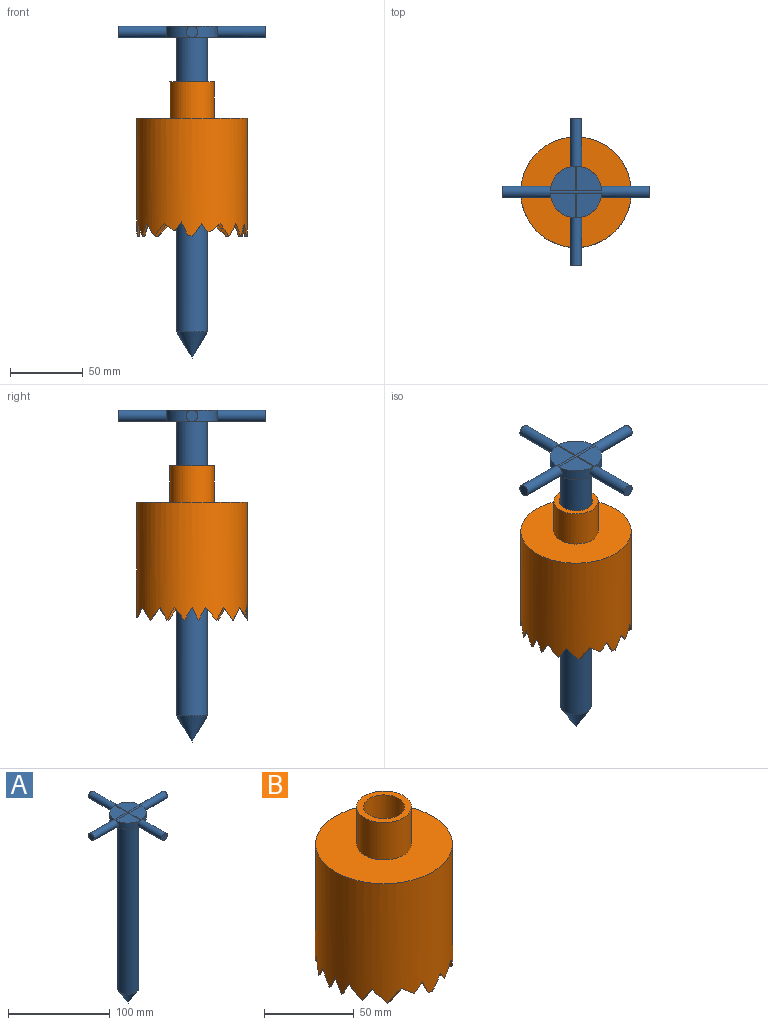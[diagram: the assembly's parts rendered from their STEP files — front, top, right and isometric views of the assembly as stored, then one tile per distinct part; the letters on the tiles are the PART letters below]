
ASSEMBLY  parts=2 mates=1
PART A: 21 faces, bbox 101.6x101.6x228.9 mm
  f0: cylinder r=10.67mm len=203.2mm, axis (0,0,-1), area 13619.6mm2, adj f9,f10,f11,f12,f13,f14,f15,f18
  f1: cylinder r=17.78mm len=17.4mm, axis (0,0,-1), area 163.7mm2, adj f7,f11,f14,f18
  f2: cylinder r=17.78mm len=17.4mm, axis (0,0,-1), area 163.7mm2, adj f8,f12,f13,f18
  f3: cylinder r=17.78mm len=17.4mm, axis (0,0,-1), area 163.7mm2, adj f6,f10,f13,f18
  f4: cylinder r=17.78mm len=17.4mm, axis (0,0,-1), area 163.7mm2, adj f5,f9,f14,f18
  f5: plane 17.4x16.82mm, normal (0,0,1), area 225.4mm2, adj f4,f14,f18
  f6: plane 17.4x16.82mm, normal (0,0,1), area 225.4mm2, adj f3,f13,f18
  f7: plane 17.4x16.82mm, normal (0,0,1), area 225.4mm2, adj f1,f14,f18
  f8: plane 17.4x16.82mm, normal (0,0,1), area 225.4mm2, adj f2,f13,f18
  f9: plane 16.45x16.32mm, normal (0,0,-1), area 139.7mm2, adj f0,f4,f14,f18
  f10: plane 16.45x16.32mm, normal (0,0,-1), area 139.7mm2, adj f0,f3,f13,f18
  f11: plane 16.45x16.32mm, normal (0,0,-1), area 139.7mm2, adj f0,f1,f14,f18
  f12: plane 16.45x16.32mm, normal (0,0,-1), area 139.7mm2, adj f0,f2,f13,f18
  f13: cylinder r=3.92mm len=49.85mm, axis (0,1,0), area 850.3mm2, adj f0,f2,f3,f6,f8,f10,f12,f16
  f14: cylinder r=3.92mm len=49.85mm, axis (0,1,0), area 850.3mm2, adj f0,f1,f4,f5,f7,f9,f11,f17
  f15: cone r=0mm half-angle=30.7deg, axis (0,0,1), area 699.5mm2, adj f0
  f16: plane 7.85x7.85mm, normal (0,-1,0), area 48.4mm2, adj f13
  f17: plane 7.85x7.85mm, normal (0,1,0), area 48.4mm2, adj f14
  f18: cylinder r=4mm len=101.6mm, axis (-1,0,0), area 1779.7mm2, adj f0,f1,f2,f3,f4,f5,f6,f7
  f19: plane 7.99x7.99mm, normal (1,0,0), area 50.2mm2, adj f18
  f20: plane 7.99x7.99mm, normal (-1,0,0), area 50.2mm2, adj f18
PART B: 53 faces, bbox 76.2x76.2x106.7 mm
  f0: plane 8.48x5.49mm, normal (0,0.86,-0.51), area 17.7mm2, adj f2,f3,f25,f51
  f1: plane 9.65x6.27mm, normal (0,0.86,-0.51), area 21mm2, adj f2,f3,f30,f50
  f2: cylinder r=38.1mm len=81.28mm, axis (0,0,-1), area 18310.4mm2, adj f0,f1,f4,f5,f6,f9,f13,f14
  f3: cylinder r=36.83mm len=76.2mm, axis (0,0,1), area 16479.2mm2, adj f0,f1,f4,f5,f6,f7,f8,f13
  f4: plane 10.91x7.39mm, normal (0,-0.92,-0.4), area 29.2mm2, adj f2,f3,f14,f46
  f5: plane 7.32x4.48mm, normal (0,-0.9,-0.44), area 15.4mm2, adj f2,f3,f44,f47
  f6: plane 5.6x3.34mm, normal (0,-0.9,-0.44), area 11.6mm2, adj f2,f3,f7,f45,f48
  f7: plane 0.13x0.06mm, normal (1,0,0), area 0mm2, adj f3,f6,f45
  f8: plane 73.66x73.66mm, normal (0,0,-1), area 3851mm2, adj f3,f12
  f9: plane 76.2x76.2mm, normal (0,0,1), area 3830.7mm2, adj f2,f10
  f10: cylinder r=15.24mm len=30.48mm, axis (0,0,-1), area 2432.2mm2, adj f9,f11
  f11: plane 30.48x30.48mm, normal (0,0,1), area 319.2mm2, adj f10,f12
  f12: cylinder r=11.43mm len=30.48mm, axis (0,0,1), area 2189mm2, adj f8,f11
  f13: plane 4.07x2.49mm, normal (0,0.86,-0.51), area 8.8mm2, adj f2,f3,f26,f52
  f14: plane 11.45x9.22mm, normal (0,0.86,-0.51), area 25.9mm2, adj f2,f3,f4,f15
  f15: plane 9.22x8.05mm, normal (0,-0.81,-0.59), area 19.9mm2, adj f2,f3,f14,f16
  f16: plane 9.22x4.67mm, normal (0,0.89,-0.45), area 15.4mm2, adj f2,f3,f15,f17
  f17: plane 9.22x5.19mm, normal (0,-0.87,-0.49), area 14.6mm2, adj f2,f3,f16,f18
  f18: plane 9.22x6.92mm, normal (0,0.8,-0.6), area 15.1mm2, adj f2,f3,f17,f19
  f19: plane 9.22x5.17mm, normal (0,-0.87,-0.49), area 13.5mm2, adj f2,f3,f18,f20
  f20: plane 9.24x4.53mm, normal (0,0.9,-0.44), area 13.1mm2, adj f2,f3,f19,f21
  f21: plane 9.22x4.67mm, normal (0,-0.89,-0.45), area 13.4mm2, adj f2,f3,f20,f22
  f22: plane 9.22x7.78mm, normal (0,0.76,-0.65), area 16.4mm2, adj f2,f3,f21,f23
  f23: plane 9.22x4.67mm, normal (0,-0.89,-0.45), area 15.3mm2, adj f2,f3,f22,f24
  f24: plane 9.22x7.88mm, normal (0,0.81,-0.59), area 19.6mm2, adj f2,f3,f23,f25
  f25: plane 9.22x8.81mm, normal (0,-0.9,-0.44), area 22.9mm2, adj f0,f2,f3,f24
  f26: plane 2.52x1.27mm, normal (-1,0,0), area 0.7mm2, adj f2,f3,f13,f31,f49
  f27: plane 11.7x8.64mm, normal (0,0.84,-0.54), area 25mm2, adj f2,f3,f28,f33
  f28: plane 3.37x0.15mm, normal (0,-0.92,-0.4), area 0.5mm2, adj f2,f3,f27,f44
  f29: plane 1.91x0.28mm, normal (0,0.8,-0.6), area 0.6mm2, adj f3,f32,f34,f35
  f30: plane 5.06x3.27mm, normal (0,-0.9,-0.44), area 8.9mm2, adj f1,f2,f3,f34
  f31: plane 2.07x1.64mm, normal (0,0.86,-0.51), area 1.9mm2, adj f3,f26,f49
  f32: plane 0.33x0.21mm, normal (-1,0,0), area 0mm2, adj f29,f34,f35
  f33: plane 8.67x7.36mm, normal (0,-0.83,-0.55), area 18.4mm2, adj f2,f3,f27,f43
  f34: plane 5.83x5.68mm, normal (0,-0.9,-0.44), area 13.2mm2, adj f2,f3,f29,f30,f32,f35
  f35: plane 8.87x6.38mm, normal (0,0.87,-0.49), area 17.3mm2, adj f2,f3,f29,f32,f34,f36
  f36: plane 8.87x5.37mm, normal (0,-0.86,-0.52), area 15.8mm2, adj f2,f3,f35,f37
  f37: plane 8.87x5.01mm, normal (0,0.87,-0.49), area 14.2mm2, adj f2,f3,f36,f38
  f38: plane 8.87x6.23mm, normal (0,-0.82,-0.57), area 14.3mm2, adj f2,f3,f37,f39
  f39: plane 8.87x4.64mm, normal (0,0.89,-0.46), area 12.8mm2, adj f2,f3,f38,f40
  f40: plane 8.88x5.5mm, normal (0,-0.85,-0.53), area 13.3mm2, adj f2,f3,f39,f41
  f41: plane 8.87x6.59mm, normal (0,0.8,-0.6), area 14.3mm2, adj f2,f3,f40,f42
  f42: plane 8.87x6.11mm, normal (0,-0.82,-0.57), area 14.6mm2, adj f2,f3,f41,f43
  f43: plane 8.87x6.96mm, normal (0,0.79,-0.62), area 16.9mm2, adj f2,f3,f33,f42
  f44: plane 3.54x0.18mm, normal (0,0.84,-0.53), area 0.7mm2, adj f2,f3,f5,f28
  f45: plane 6.73x5.2mm, normal (-0.79,0,-0.61), area 8.8mm2, adj f2,f3,f6,f7,f46
  f46: plane 6.69x3.88mm, normal (0.87,0,-0.5), area 8.1mm2, adj f2,f3,f4,f45
  f47: plane 4.34x2.73mm, normal (-0.85,0,-0.53), area 5.1mm2, adj f2,f3,f5,f48
  f48: plane 6.56x3.1mm, normal (0.9,0,-0.43), area 7.2mm2, adj f2,f3,f6,f47
  f49: plane 8.54x6.79mm, normal (0.78,0,-0.62), area 12.4mm2, adj f2,f3,f26,f31,f50
  f50: plane 5.95x4.21mm, normal (-0.82,0,-0.58), area 8.2mm2, adj f1,f2,f3,f49
  f51: plane 6.25x4.76mm, normal (0.8,0,-0.61), area 9mm2, adj f0,f2,f3,f52
  f52: plane 9.28x4.22mm, normal (-0.91,0,-0.41), area 11.5mm2, adj f2,f3,f13,f51
PLACE A t=(149.51,14.41,-186.05)mm
PLACE B t=(149.51,14.41,-120.16)mm
MATE slider B.f12 <-> A.f0  axis (0,0,1) through (149.51,14.41,-28.72)mm
